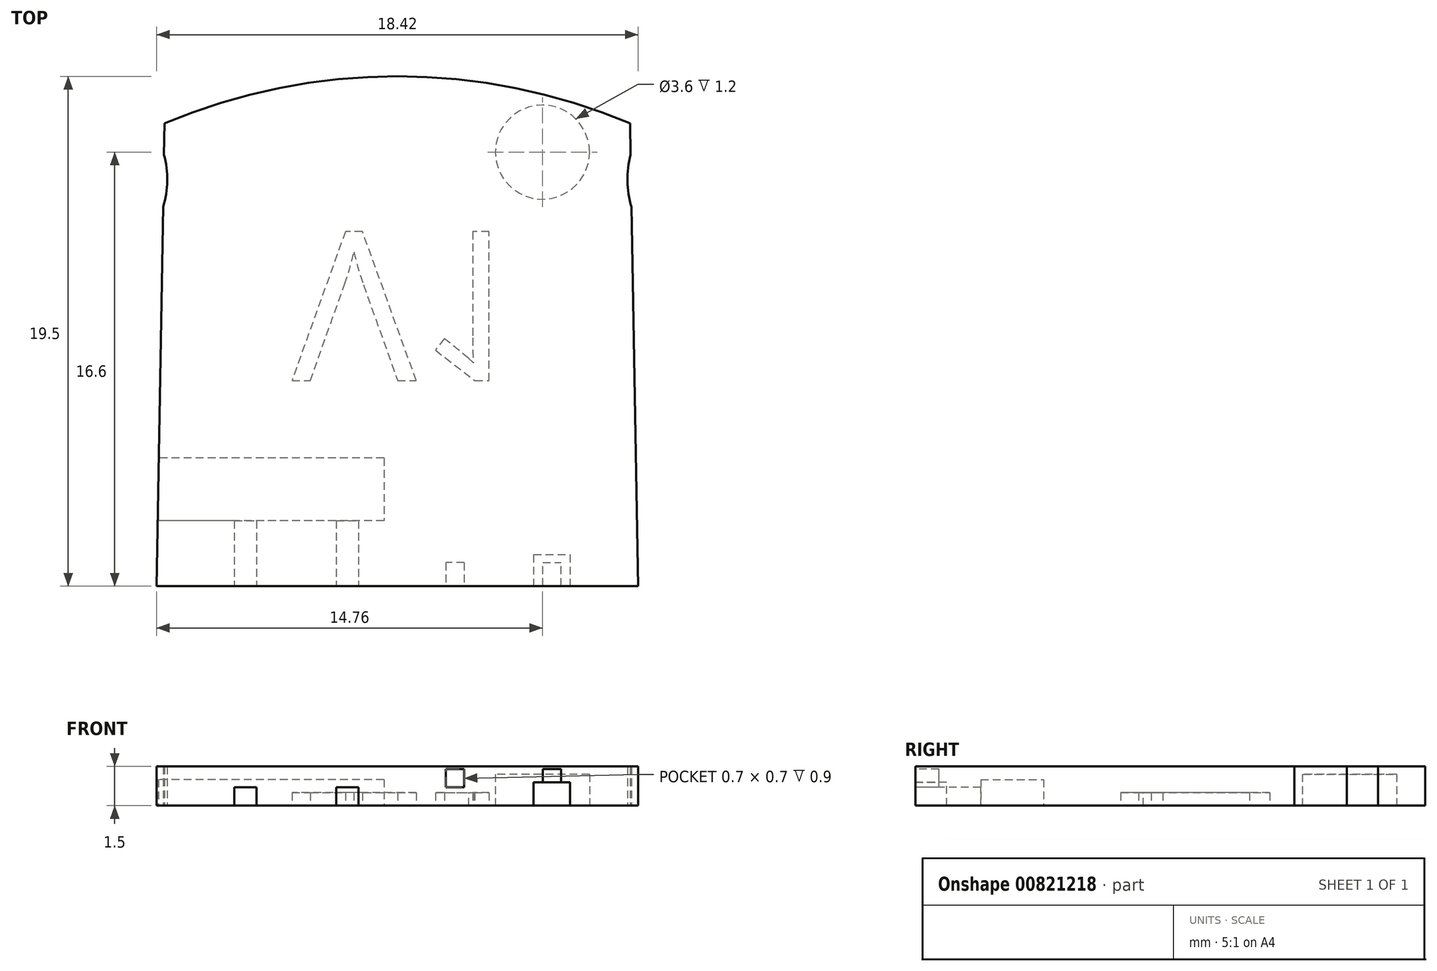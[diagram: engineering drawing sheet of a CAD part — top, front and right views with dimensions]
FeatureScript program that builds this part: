
annotation { "Feature Type Name" : "Feature", "Feature Type Description" : "" }
export const myFeature = defineFeature(function(context is Context, id is Id, definition is map)
    precondition{}
    {
        {
            var Q0;
            Q0=qCreatedBy(makeId("Top.planeOp"),FACE);
            var sketch = newSketch(context, id + "F0", { "sketchPlane" : qUnion([Q0])});
            skLineSegment(sketch, "E0", {"start": v(-9.2, 0) * mm, "end": v(9.21, 0) * mm});
            skLineSegment(sketch, "E1", {"start": v(-9.21, 0) * mm, "end": v(-8.9, 17.7) * mm});
            skLineSegment(sketch, "E2", {"start": v(-8.9, 17.7) * mm, "end": v(8.9, 17.7) * mm});
            skLineSegment(sketch, "E3", {"start": v(8.9, 17.7) * mm, "end": v(9.21, 0) * mm});
            skPoint(sketch, "E4", {"position": v(0, 19.5) * mm});
            skArc(sketch, "E5", {"start": v(8.9, 17.7) * mm, "mid": v(0, 19.5) * mm, "end": v(-8.9, 17.7) * mm});
            skPoint(sketch, "E6", {"position": v(-8.96, 14.5) * mm});
            skPoint(sketch, "E7", {"position": v(-8.92, 16.5) * mm});
            skPoint(sketch, "E8", {"position": v(-8.8, 15.5) * mm});
            skArc(sketch, "E9", {"start": v(-8.96, 14.5) * mm, "mid": v(-8.8, 15.5) * mm, "end": v(-8.92, 16.5) * mm});
            skArc(sketch, "E10.MirrorCS", {"start": v(8.96, 14.5) * mm, "mid": v(8.8, 15.5) * mm, "end": v(8.92, 16.5) * mm});
            skSolve(sketch);
        }
        {
            var Q0;
            {var subQ4=sQuery(id+"F0.wireOp",EDGE,"E0");Q0=makeQuery(id+"F0.imprint","IMPRINT",FACE,{"disambiguationData":[TD([[makeQuery(id+"F0.imprint","IMPRINT",EDGE,{"derivedFrom":subQ4}),1.0]])]});}
            var Q1;
            Q1=makeQuery(id+"F0.imprint","IMPRINT",FACE,{"disambiguationData":[TD([[makeQuery(id+"F0.imprint","IMPRINT",EDGE,{"derivedFrom":sQuery(id+"F0.wireOp",EDGE,"E2")}),1.0]])]});
            extrude(context, id + "F1", {"entities" : qUnion([Q0, Q1]), "depth" : 1.5 * mm, "offsetDistance" : 25 * mm});
        }
        {
            var Q0;
            Q0=qCreatedBy(makeId("Top.planeOp"),FACE);
            var sketch = newSketch(context, id + "F2", { "sketchPlane" : qUnion([Q0])});
            skLineSegment(sketch, "E11", {"start": v(5.55, 21.02) * mm, "end": v(5.55, -2.21) * mm, "construction": true});
            skLineSegment(sketch, "E12", {"start": v(13.66, 16.6) * mm, "end": v(-14.4, 16.6) * mm, "construction": true});
            skCircle(sketch, "E13", {"center": v(5.55, 16.6) * mm, "radius": 1.8 * mm});
            skCircle(sketch, "E14.MirrorC", {"center": v(-5.55, 16.6) * mm, "radius": 1.8 * mm});
            skSolve(sketch);
        }
        {
            var Q0;
            Q0=makeQuery(id+"F2.imprint","IMPRINT",FACE,{"disambiguationData":[TD([[makeQuery(id+"F2.imprint","IMPRINT",EDGE,{"derivedFrom":sQuery(id+"F2.wireOp",EDGE,"E13")}),1.0]])]});
            var Q1;
            Q1=makeQuery(id+"F2.imprint","IMPRINT",FACE,{"disambiguationData":[TD([[makeQuery(id+"F2.imprint","IMPRINT",EDGE,{"derivedFrom":sQuery(id+"F2.wireOp",EDGE,"E14.MirrorC")}),-1.0]])]});
            extrude(context, id + "F3", {"entities" : qUnion([Q0, Q1]), "operationType" : NewBodyOperationType.REMOVE, "depth" : 1.2 * mm, "offsetDistance" : 25 * mm});
        }
        {
            var Q0;
            Q0=makeQuery(id+"F1.opExtrude","CAP_FACE",FACE,{"disambiguationData":[OSD([sQuery(id+"F0.wireOp",EDGE,"E0"),sQuery(id+"F0.wireOp",EDGE,"E1"),sQuery(id+"F0.wireOp",EDGE,"E3"),sQuery(id+"F0.wireOp",EDGE,"E5"),sQuery(id+"F0.wireOp",EDGE,"E9"),sQuery(id+"F0.wireOp",EDGE,"E10.MirrorCS")])],"isStart":true});
            var sketch = newSketch(context, id + "F4", { "sketchPlane" : qUnion([Q0])});
            skLineSegment(sketch, "E15", {"start": v(9.68, -4.9) * mm, "end": v(-12.52, -4.9) * mm});
            skLineSegment(sketch, "E16", {"start": v(9.86, -2.5) * mm, "end": v(-11.55, -2.5) * mm});
            skLineSegment(sketch, "E17", {"start": v(-0.51, -9.35) * mm, "end": v(-0.51, 2.72) * mm});
            skLineSegment(sketch, "E18", {"start": v(-9.2, 0) * mm, "end": v(-9.2, -15.18) * mm});
            skSolve(sketch);
        }
        {
            var Q0;
            {var subQ0=sQuery(id+"F4.wireOp",EDGE,"E17");var subQ1=sQuery(id+"F4.wireOp",EDGE,"E15");var subQ2=makeQuery(id+"F4.imprint","INTERSECT",VERTEX,{"derivedFrom":[subQ1,subQ0]});Q0=makeQuery(id+"F4.imprint","IMPRINT",FACE,{"disambiguationData":[TD([[makeQuery(id+"F4.imprint","IMPRINT",EDGE,{"disambiguationData":[TD([[subQ2,-1.0]])],"derivedFrom":subQ0}),1.0]])]});}
            extrude(context, id + "F5", {"entities" : qUnion([Q0]), "operationType" : NewBodyOperationType.REMOVE, "oppositeDirection" : true, "depth" : 1 * mm, "offsetDistance" : 25 * mm});
        }
        {
            var Q0;
            Q0=makeQuery(id+"F1.opExtrude","CAP_FACE",FACE,{"disambiguationData":[OSD([sQuery(id+"F0.wireOp",EDGE,"E0"),sQuery(id+"F0.wireOp",EDGE,"E1"),sQuery(id+"F0.wireOp",EDGE,"E3"),sQuery(id+"F0.wireOp",EDGE,"E5"),sQuery(id+"F0.wireOp",EDGE,"E9"),sQuery(id+"F0.wireOp",EDGE,"E10.MirrorCS")])],"isStart":true});
            var sketch = newSketch(context, id + "F6", { "sketchPlane" : qUnion([Q0])});
            skLineSegment(sketch, "E19", {"start": v(-1.9, -5.79) * mm, "end": v(-1.91, 3.18) * mm, "construction": true});
            skLineSegment(sketch, "E20", {"start": v(-5.8, -6) * mm, "end": v(-5.81, 2.5) * mm, "construction": true});
            skLineSegment(sketch, "E21", {"start": v(13.46, -1.75) * mm, "end": v(-21.1, -1.75) * mm, "construction": true});
            skLineSegment(sketch, "E22.bottom", {"start": v(-1.48, -3.75) * mm, "end": v(-2.33, -3.75) * mm});
            skLineSegment(sketch, "E22.top", {"start": v(-1.48, 0.25) * mm, "end": v(-2.33, 0.25) * mm});
            skLineSegment(sketch, "E22.left", {"start": v(-1.48, -3.75) * mm, "end": v(-1.48, 0.25) * mm});
            skLineSegment(sketch, "E22.right", {"start": v(-2.33, -3.75) * mm, "end": v(-2.33, 0.25) * mm});
            skPoint(sketch, "E22.middle", {"position": v(-1.9, -1.75) * mm});
            skLineSegment(sketch, "E23.bottom", {"start": v(-5.38, -3.75) * mm, "end": v(-6.23, -3.75) * mm});
            skLineSegment(sketch, "E23.top", {"start": v(-5.38, 0.25) * mm, "end": v(-6.23, 0.25) * mm});
            skLineSegment(sketch, "E23.left", {"start": v(-5.38, -3.75) * mm, "end": v(-5.38, 0.25) * mm});
            skLineSegment(sketch, "E23.right", {"start": v(-6.23, -3.75) * mm, "end": v(-6.23, 0.25) * mm});
            skPoint(sketch, "E23.middle", {"position": v(-5.8, -1.75) * mm});
            skSolve(sketch);
        }
        {
            var Q0;
            {var subQ0=sQuery(id+"F6.wireOp",EDGE,"E22.left");var subQ1=makeQuery(id+"F5.boolean.opBoolean","COPY",EDGE,{"derivedFrom":makeQuery(id+"F5.opExtrude","CAP_EDGE",EDGE,{"disambiguationData":[OSD([sQuery(id+"F4.wireOp",EDGE,"E16")])],"isStart":true})});var subQ2=makeQuery(id+"F6.imprint","INTERSECT",VERTEX,{"derivedFrom":[subQ1,subQ0]});Q0=makeQuery(id+"F6.imprint","IMPRINT",FACE,{"disambiguationData":[TD([[makeQuery(id+"F6.imprint","IMPRINT",EDGE,{"disambiguationData":[TD([[subQ2,-1.0]])],"derivedFrom":subQ0}),1.0]])]});}
            var Q1;
            {var subQ0=sQuery(id+"F6.wireOp",EDGE,"E23.left");var subQ1=makeQuery(id+"F5.boolean.opBoolean","COPY",EDGE,{"derivedFrom":makeQuery(id+"F5.opExtrude","CAP_EDGE",EDGE,{"disambiguationData":[OSD([sQuery(id+"F4.wireOp",EDGE,"E16")])],"isStart":true})});var subQ2=makeQuery(id+"F6.imprint","INTERSECT",VERTEX,{"derivedFrom":[subQ1,subQ0]});Q1=makeQuery(id+"F6.imprint","IMPRINT",FACE,{"disambiguationData":[TD([[makeQuery(id+"F6.imprint","IMPRINT",EDGE,{"disambiguationData":[TD([[subQ2,-1.0]])],"derivedFrom":subQ0}),1.0]])]});}
            extrude(context, id + "F7", {"entities" : qUnion([Q0, Q1]), "operationType" : NewBodyOperationType.REMOVE, "oppositeDirection" : true, "depth" : 0.7 * mm, "offsetDistance" : 25 * mm});
        }
        {
            var Q0;
            Q0=makeQuery(id+"F1.opExtrude","SWEPT_FACE",FACE,{"disambiguationData":[OSD([sQuery(id+"F0.wireOp",EDGE,"E0")])]});
            var sketch = newSketch(context, id + "F8", { "sketchPlane" : qUnion([Q0])});
            skLineSegment(sketch, "E24", {"start": v(5.91, -2.14) * mm, "end": v(5.9, 4.32) * mm, "construction": true});
            skLineSegment(sketch, "E25", {"start": v(2.11, -2.11) * mm, "end": v(2.11, 4.26) * mm, "construction": true});
            skLineSegment(sketch, "E26.0", {"start": v(-1.48, 0) * mm, "end": v(9.21, 0) * mm});
            skLineSegment(sketch, "E27", {"start": v(9.7, 0.9) * mm, "end": v(0.57, 0.9) * mm});
            skLineSegment(sketch, "E28", {"start": v(5.91, 0) * mm, "end": v(5.91, 1.2) * mm});
            skLineSegment(sketch, "E29", {"start": v(6.61, 0) * mm, "end": v(6.61, 0.9) * mm});
            skLineSegment(sketch, "E30", {"start": v(5.21, 0) * mm, "end": v(5.21, 0.9) * mm});
            skLineSegment(sketch, "E31", {"start": v(9.67, 1.2) * mm, "end": v(2.64, 1.2) * mm});
            skLineSegment(sketch, "E32.bottom", {"start": v(2.81, 0) * mm, "end": v(2.11, 0) * mm});
            skLineSegment(sketch, "E32.top", {"start": v(2.81, 0.9) * mm, "end": v(2.11, 0.9) * mm});
            skLineSegment(sketch, "E32.left", {"start": v(2.81, 0) * mm, "end": v(2.81, 0.9) * mm});
            skLineSegment(sketch, "E32.right", {"start": v(2.11, 0) * mm, "end": v(2.11, 0.9) * mm});
            skLineSegment(sketch, "E33.bottom", {"start": v(2.11, 0) * mm, "end": v(1.41, 0) * mm});
            skLineSegment(sketch, "E33.top", {"start": v(2.11, 0.9) * mm, "end": v(1.41, 0.9) * mm});
            skLineSegment(sketch, "E33.right", {"start": v(1.41, 0) * mm, "end": v(1.41, 0.9) * mm});
            skSolve(sketch);
        }
        {
            var Q0;
            {var subQ3=sQuery(id+"F8.wireOp",EDGE,"E29");Q0=makeQuery(id+"F8.imprint","IMPRINT",FACE,{"disambiguationData":[TD([[makeQuery(id+"F8.imprint","IMPRINT",EDGE,{"derivedFrom":subQ3}),1.0]])]});}
            var Q1;
            {var subQ3=sQuery(id+"F8.wireOp",EDGE,"E30");Q1=makeQuery(id+"F8.imprint","IMPRINT",FACE,{"disambiguationData":[TD([[makeQuery(id+"F8.imprint","IMPRINT",EDGE,{"derivedFrom":subQ3}),-1.0]])]});}
            var Q2;
            Q2=makeQuery(id+"F8.imprint","IMPRINT",FACE,{"disambiguationData":[TD([[makeQuery(id+"F8.imprint","IMPRINT",EDGE,{"derivedFrom":sQuery(id+"F8.wireOp",EDGE,"E33.bottom")}),1.0]])]});
            var Q3;
            Q3=makeQuery(id+"F8.imprint","IMPRINT",FACE,{"disambiguationData":[TD([[makeQuery(id+"F8.imprint","IMPRINT",EDGE,{"derivedFrom":sQuery(id+"F8.wireOp",EDGE,"E32.bottom")}),1.0]])]});
            extrude(context, id + "F9", {"entities" : qUnion([Q0, Q1, Q2, Q3]), "operationType" : NewBodyOperationType.REMOVE, "oppositeDirection" : true, "depth" : 1.2 * mm, "offsetDistance" : 25 * mm});
        }
        {
            var Q0;
            Q0=makeQuery(id+"F1.opExtrude","SWEPT_FACE",FACE,{"disambiguationData":[OSD([sQuery(id+"F0.wireOp",EDGE,"E0")])]});
            var sketch = newSketch(context, id + "F10", { "sketchPlane" : qUnion([Q0])});
            skLineSegment(sketch, "E34", {"start": v(5.91, -2.14) * mm, "end": v(5.91, 4.32) * mm, "construction": true});
            skLineSegment(sketch, "E35", {"start": v(2.21, -2.11) * mm, "end": v(2.21, 4.26) * mm, "construction": true});
            skLineSegment(sketch, "E36.0", {"start": v(-1.3, 0) * mm, "end": v(9.21, 0) * mm});
            skLineSegment(sketch, "E37", {"start": v(9.7, 0.9) * mm, "end": v(6.61, 0.9) * mm});
            skLineSegment(sketch, "E38", {"start": v(6.06, 0.9) * mm, "end": v(6.06, 1.2) * mm});
            skLineSegment(sketch, "E39", {"start": v(6.61, 0) * mm, "end": v(6.61, 0.9) * mm});
            skLineSegment(sketch, "E40", {"start": v(5.76, 0.9) * mm, "end": v(5.76, 1.2) * mm});
            skLineSegment(sketch, "E41", {"start": v(5.21, 0) * mm, "end": v(5.21, 0.9) * mm});
            skLineSegment(sketch, "E42", {"start": v(6.06, 1.2) * mm, "end": v(5.76, 1.2) * mm});
            skLineSegment(sketch, "E43.bottom", {"start": v(2.91, 0) * mm, "end": v(2.36, 0) * mm});
            skLineSegment(sketch, "E43.left", {"start": v(2.91, 0) * mm, "end": v(2.91, 0.9) * mm});
            skLineSegment(sketch, "E43.right", {"start": v(2.36, 0.9) * mm, "end": v(2.36, 1.2) * mm});
            skLineSegment(sketch, "E44.bottom", {"start": v(2.06, 0) * mm, "end": v(1.51, 0) * mm});
            skLineSegment(sketch, "E44.left", {"start": v(2.06, 0.9) * mm, "end": v(2.06, 1.2) * mm});
            skLineSegment(sketch, "E44.right", {"start": v(1.51, 0) * mm, "end": v(1.51, 0.9) * mm});
            skPoint(sketch, "E45.orphan", {"position": v(6.06, 0) * mm});
            skPoint(sketch, "E46.orphan", {"position": v(5.76, 0) * mm});
            skLineSegment(sketch, "E47.trimOffspring", {"start": v(1.51, 0.9) * mm, "end": v(0.57, 0.9) * mm});
            skLineSegment(sketch, "E48.trimOffspring", {"start": v(2.36, 1.2) * mm, "end": v(2.06, 1.2) * mm});
            skPoint(sketch, "E49.orphan", {"position": v(0, 1.2) * mm});
            skLineSegment(sketch, "E50.trimOffspring", {"start": v(2.36, 0.9) * mm, "end": v(2.06, 0.9) * mm});
            skLineSegment(sketch, "E51.0", {"start": v(2.56, 0.7) * mm, "end": v(1.86, 0.7) * mm});
            skLineSegment(sketch, "E51.1", {"start": v(2.56, 0.7) * mm, "end": v(2.56, 1.4) * mm});
            skLineSegment(sketch, "E51.2", {"start": v(2.56, 1.4) * mm, "end": v(1.86, 1.4) * mm});
            skLineSegment(sketch, "E51.3", {"start": v(1.86, 0.7) * mm, "end": v(1.86, 1.4) * mm});
            skLineSegment(sketch, "E52.trimOffspring", {"start": v(6.06, 0.9) * mm, "end": v(5.76, 0.9) * mm});
            skLineSegment(sketch, "E53.trimOffspring", {"start": v(5.21, 0.9) * mm, "end": v(2.91, 0.9) * mm});
            skLineSegment(sketch, "E54.0", {"start": v(6.26, 0.7) * mm, "end": v(5.56, 0.7) * mm});
            skLineSegment(sketch, "E54.1", {"start": v(6.26, 0.7) * mm, "end": v(6.26, 1.4) * mm});
            skLineSegment(sketch, "E54.2", {"start": v(6.26, 1.4) * mm, "end": v(5.56, 1.4) * mm});
            skLineSegment(sketch, "E54.3", {"start": v(5.56, 0.7) * mm, "end": v(5.56, 1.4) * mm});
            skSolve(sketch);
        }
        {
            var Q0;
            Q0=makeQuery(id+"F10.imprint","IMPRINT",FACE,{"disambiguationData":[TD([[makeQuery(id+"F10.imprint","IMPRINT",EDGE,{"derivedFrom":sQuery(id+"F10.wireOp",EDGE,"E43.right")}),1.0]])]});
            var Q1;
            {var subQ0=sQuery(id+"F10.wireOp",EDGE,"E51.1");var subQ1=sQuery(id+"F10.wireOp",EDGE,"E51.0");var subQ2=makeQuery(id+"F10.imprint","INTERSECT",VERTEX,{"derivedFrom":[subQ1,subQ0]});Q1=makeQuery(id+"F10.imprint","IMPRINT",FACE,{"disambiguationData":[TD([[makeQuery(id+"F10.imprint","IMPRINT",EDGE,{"disambiguationData":[TD([[subQ2,-1.0]])],"derivedFrom":subQ1}),-1.0]])]});}
            var Q2;
            {var subQ0=sQuery(id+"F10.wireOp",EDGE,"E50.trimOffspring");Q2=makeQuery(id+"F10.imprint","IMPRINT",FACE,{"disambiguationData":[TD([[makeQuery(id+"F10.imprint","IMPRINT",EDGE,{"derivedFrom":subQ0}),1.0]])]});}
            var Q3;
            {var subQ0=sQuery(id+"F10.wireOp",EDGE,"E51.3");var subQ1=sQuery(id+"F10.wireOp",EDGE,"E51.0");var subQ2=makeQuery(id+"F10.imprint","INTERSECT",VERTEX,{"derivedFrom":[subQ1,subQ0]});Q3=makeQuery(id+"F10.imprint","IMPRINT",FACE,{"disambiguationData":[TD([[makeQuery(id+"F10.imprint","IMPRINT",EDGE,{"disambiguationData":[TD([[subQ2,1.0]])],"derivedFrom":subQ1}),-1.0]])]});}
            var Q4;
            {var subQ8=sQuery(id+"F10.wireOp",EDGE,"E43.right");Q4=makeQuery(id+"F10.imprint","IMPRINT",FACE,{"disambiguationData":[TD([[makeQuery(id+"F10.imprint","IMPRINT",EDGE,{"derivedFrom":subQ8}),-1.0]])]});}
            var Q5;
            {var subQ12=sQuery(id+"F10.wireOp",EDGE,"E38");Q5=makeQuery(id+"F10.imprint","IMPRINT",FACE,{"disambiguationData":[TD([[makeQuery(id+"F10.imprint","IMPRINT",EDGE,{"derivedFrom":subQ12}),-1.0]])]});}
            var Q6;
            Q6=makeQuery(id+"F10.imprint","IMPRINT",FACE,{"disambiguationData":[TD([[makeQuery(id+"F10.imprint","IMPRINT",EDGE,{"derivedFrom":sQuery(id+"F10.wireOp",EDGE,"E38")}),1.0]])]});
            var Q7;
            {var subQ0=sQuery(id+"F10.wireOp",EDGE,"E52.trimOffspring");Q7=makeQuery(id+"F10.imprint","IMPRINT",FACE,{"disambiguationData":[TD([[makeQuery(id+"F10.imprint","IMPRINT",EDGE,{"derivedFrom":subQ0}),1.0]])]});}
            var Q8;
            {var subQ0=sQuery(id+"F10.wireOp",EDGE,"E54.1");var subQ1=sQuery(id+"F10.wireOp",EDGE,"E54.0");var subQ2=makeQuery(id+"F10.imprint","INTERSECT",VERTEX,{"derivedFrom":[subQ1,subQ0]});Q8=makeQuery(id+"F10.imprint","IMPRINT",FACE,{"disambiguationData":[TD([[makeQuery(id+"F10.imprint","IMPRINT",EDGE,{"disambiguationData":[TD([[subQ2,-1.0]])],"derivedFrom":subQ1}),-1.0]])]});}
            var Q9;
            {var subQ0=sQuery(id+"F10.wireOp",EDGE,"E54.3");var subQ1=sQuery(id+"F10.wireOp",EDGE,"E54.0");var subQ2=makeQuery(id+"F10.imprint","INTERSECT",VERTEX,{"derivedFrom":[subQ1,subQ0]});Q9=makeQuery(id+"F10.imprint","IMPRINT",FACE,{"disambiguationData":[TD([[makeQuery(id+"F10.imprint","IMPRINT",EDGE,{"disambiguationData":[TD([[subQ2,1.0]])],"derivedFrom":subQ1}),-1.0]])]});}
            extrude(context, id + "F11", {"entities" : qUnion([Q0, Q1, Q2, Q3, Q4, Q5, Q6, Q7, Q8, Q9]), "operationType" : NewBodyOperationType.REMOVE, "oppositeDirection" : true, "depth" : 0.9 * mm, "offsetDistance" : 25 * mm});
        }
        {
            var Q0;
            {var subQ0=sQuery(id+"F0.wireOp",EDGE,"E9");var subQ1=sQuery(id+"F0.wireOp",EDGE,"E10.MirrorCS");var subQ2=sQuery(id+"F0.wireOp",EDGE,"E5");var subQ3=sQuery(id+"F0.wireOp",EDGE,"E3");var subQ4=sQuery(id+"F0.wireOp",EDGE,"E0");var subQ6=sQuery(id+"F0.wireOp",EDGE,"E1");Q0=makeQuery(id+"F7.boolean.opBoolean","SPLIT",FACE,{"disambiguationData":[TD([makeQuery(id+"F1.opExtrude","SWEPT_FACE",FACE,{"disambiguationData":[OSD([subQ2])]})])],"derivedFrom":makeQuery(id+"F1.opExtrude","CAP_FACE",FACE,{"disambiguationData":[OSD([subQ4,subQ6,subQ3,subQ2,subQ0,subQ1])],"isStart":true})});}
            var sketch = newSketch(context, id + "F12", { "sketchPlane" : qUnion([Q0])});
            skText(sketch, "E55", { "text": "V1", "fontName": "OpenSans-Regular.ttf"});
            const initialGuessF12  = {"E55": [-0.00403, -0.01356, 1, 0, 0.00575]};
            skSetInitialGuess(sketch, initialGuessF12);
            skSolve(sketch);
        }
        {
            var Q0;
            Q0 = qSketchRegion(id + "F12", true);
            extrude(context, id + "F13", {"entities" : qUnion([Q0]), "operationType" : NewBodyOperationType.REMOVE, "oppositeDirection" : true, "depth" : 0.5 * mm, "offsetDistance" : 25 * mm});
        }
    });
